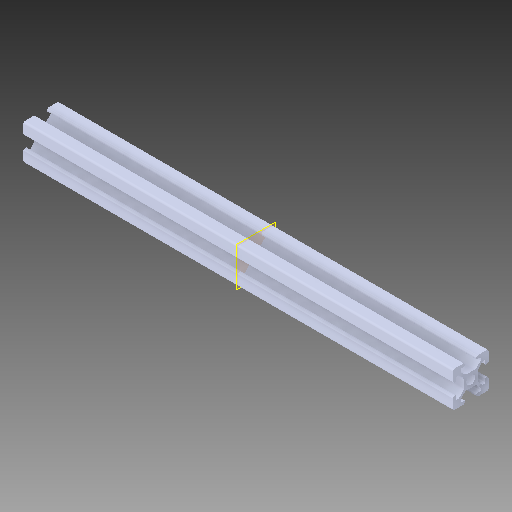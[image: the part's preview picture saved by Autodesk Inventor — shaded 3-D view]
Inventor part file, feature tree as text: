
AUTODESK INVENTOR PART (.ipt)
format: ipt  version: 2018 (Build 220112000, 112)  size: 382,464 bytes
history: native  units: in
note: dims shown in document units (in); Inventor stores cm internally (conversion verified against a paired STEP export)
features: extrude x1, plane x1, sketch x1, projected_geometry x1, fillet x1
ambient origin geometry x8: Origin, YZ Plane, XZ Plane, XY Plane, X Axis, Y Axis, Z Axis, Center Point
bodies: Solid1 (feature_tree)
feature tree (5):
  extrude  "Extrusion2"  [1 undecoded]
  plane  "Work Plane1"
  sketch  "Sketch3"  dims[d2=5.5118in d3=0.0in]
  projected_geometry  "Projected Loop2"
  fillet  "Fillet5"  [1 undecoded]
note: 2 required parameter values undecoded (feature->parameter linkage not recoverable at this tier; creation-order binding heuristic only, values carry confidence <= 0.55)
